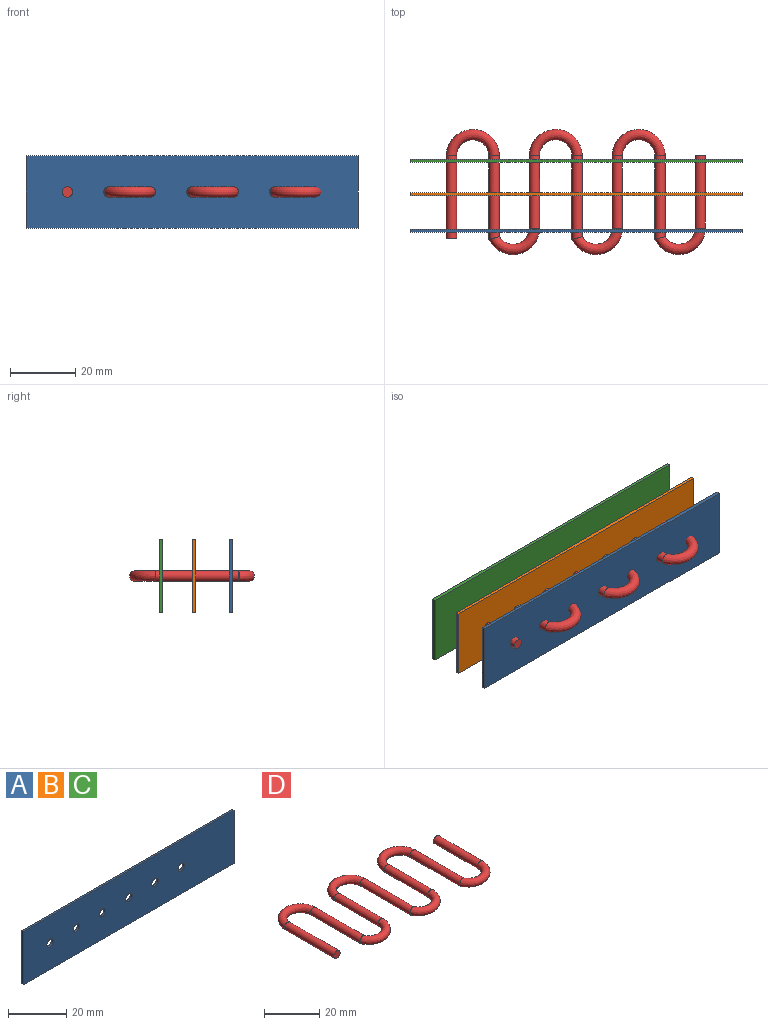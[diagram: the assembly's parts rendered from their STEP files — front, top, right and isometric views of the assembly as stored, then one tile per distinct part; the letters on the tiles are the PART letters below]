
ASSEMBLY  parts=4 mates=3
PART A: 12 faces, bbox 101.7x1x22.3 mm
  f0: plane 22.31x0.95mm, normal (-1,0,0), area 21.3mm2, adj f1,f3,f4,f5
  f1: plane 101.71x0.95mm, normal (0,0,-1), area 96.9mm2, adj f0,f2,f4,f5
  f2: plane 22.31x0.95mm, normal (1,0,0), area 21.3mm2, adj f1,f3,f4,f5
  f3: plane 101.71x0.95mm, normal (0,0,1), area 96.9mm2, adj f0,f2,f4,f5
  f4: plane 101.71x22.31mm, normal (0,-1,0), area 2221.6mm2, adj f0,f1,f2,f3,f6,f7,f8,f9
  f5: plane 101.71x22.31mm, normal (0,1,0), area 2221.6mm2, adj f0,f1,f2,f3,f6,f7,f8,f9
  f6: cylinder r=1.59mm len=3.18mm, axis (0,-1,0), area 9.5mm2, adj f4,f5
  f7: cylinder r=1.59mm len=3.18mm, axis (0,-1,0), area 9.5mm2, adj f4,f5
  f8: cylinder r=1.59mm len=3.18mm, axis (0,-1,0), area 9.5mm2, adj f4,f5
  f9: cylinder r=1.59mm len=3.18mm, axis (0,-1,0), area 9.5mm2, adj f4,f5
  f10: cylinder r=1.59mm len=3.18mm, axis (0,-1,0), area 9.5mm2, adj f4,f5
  f11: cylinder r=1.59mm len=3.18mm, axis (0,-1,0), area 9.5mm2, adj f4,f5
PART B: same geometry as A
PART C: same geometry as A
PART D: 15 faces, bbox 81x41.8x3.2 mm
  f0: plane 3.18x3.18mm, normal (0,1,0), area 7.9mm2, adj f3
  f1: plane 3.18x3.18mm, normal (0,-1,0), area 7.9mm2, adj f14
  f2: bspline ~15.29x8.11mm, area 173.2mm2, adj f3,f5
  f3: cylinder r=1.59mm len=22.34mm, axis (0,1,0), area 222.9mm2, adj f0,f2
  f4: bspline ~19.43x9.83mm, area 204.3mm2, adj f5,f7
  f5: cylinder r=1.59mm len=25.14mm, axis (0,-1,0), area 250.8mm2, adj f2,f4
  f6: bspline ~18.61x9.95mm, area 173.3mm2, adj f7,f9
  f7: cylinder r=1.59mm len=22.2mm, axis (0,1,0), area 220.9mm2, adj f4,f6
  f8: bspline ~19.43x9.83mm, area 204.3mm2, adj f9,f11
  f9: cylinder r=1.59mm len=25.14mm, axis (0,-1,0), area 250.8mm2, adj f6,f8
  f10: bspline ~18.61x9.95mm, area 173.3mm2, adj f11,f13
  f11: cylinder r=1.59mm len=22.2mm, axis (0,1,0), area 220.9mm2, adj f8,f10
  f12: bspline ~19.43x9.83mm, area 204.3mm2, adj f13,f14
  f13: cylinder r=1.59mm len=25.14mm, axis (0,-1,0), area 250.8mm2, adj f10,f12
  f14: cylinder r=1.59mm len=25.25mm, axis (0,1,0), area 251.2mm2, adj f1,f12
PLACE A t=(3.1,-25.64,-19.24)mm
PLACE B t=(3.1,-14.47,-19.24)mm
PLACE C t=(3.1,-4.26,-19.24)mm
PLACE D t=(15.8,-28.38,-8.08)mm
MATE cylindrical D.f14 <-> C.f11  axis (0,1,0) through (15.8,-15.68,-8.08)mm
MATE cylindrical B.f11 <-> D.f14  axis (0,-1,0) through (15.8,-14.95,-8.08)mm
MATE cylindrical A.f11 <-> D.f14  axis (0,-1,0) through (15.8,-26.59,-8.08)mm
